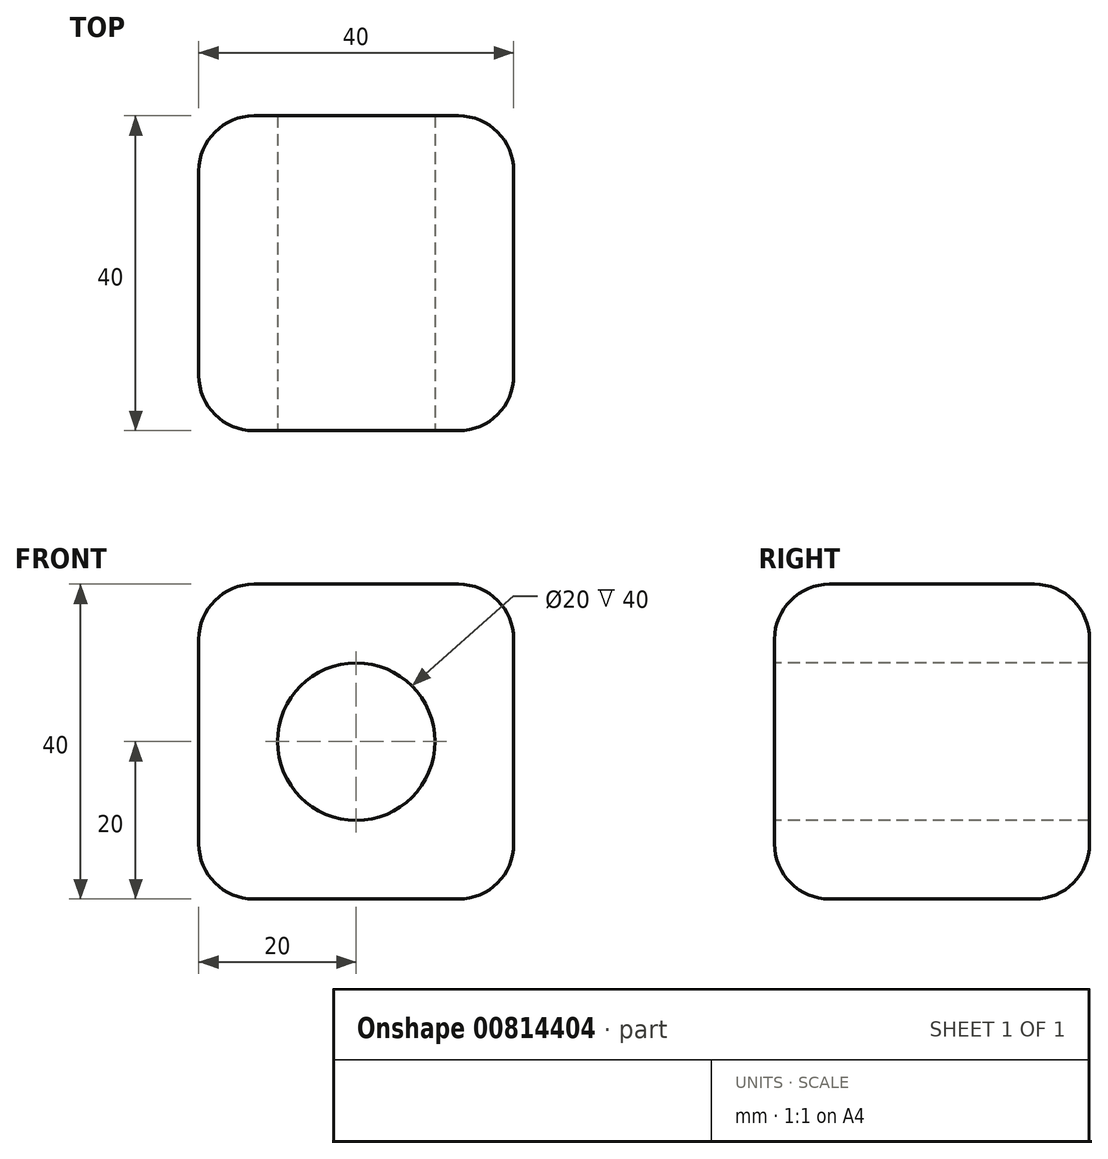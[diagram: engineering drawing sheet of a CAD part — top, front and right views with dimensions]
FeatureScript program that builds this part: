
annotation { "Feature Type Name" : "Feature", "Feature Type Description" : "" }
export const myFeature = defineFeature(function(context is Context, id is Id, definition is map)
    precondition{}
    {
        {
            var Q0;
            Q0=qCreatedBy(makeId("Front.planeOp"),FACE);
            var sketch = newSketch(context, id + "F0", { "sketchPlane" : qUnion([Q0])});
            skLineSegment(sketch, "E0.bottom", {"start": v(0, 40) * mm, "end": v(40, 40) * mm});
            skLineSegment(sketch, "E0.top", {"start": v(0, 0) * mm, "end": v(40, 0) * mm});
            skLineSegment(sketch, "E0.left", {"start": v(0, 40) * mm, "end": v(0, 0) * mm});
            skLineSegment(sketch, "E0.right", {"start": v(40, 40) * mm, "end": v(40, 0) * mm});
            skSolve(sketch);
        }
        {
            var Q0;
            Q0=makeQuery(id+"F0.imprint","IMPRINT",FACE,{"disambiguationData":[TD([[makeQuery(id+"F0.imprint","IMPRINT",EDGE,{"derivedFrom":sQuery(id+"F0.wireOp",EDGE,"E0.bottom")}),-1.0]])]});
            extrude(context, id + "F1", {"entities" : qUnion([Q0]), "depth" : 40 * mm, "offsetDistance" : 25 * mm});
        }
        {
            var Q0;
            Q0=makeQuery(id+"F1.opExtrude","SWEPT_FACE",FACE,{"disambiguationData":[OSD([sQuery(id+"F0.wireOp",EDGE,"E0.bottom")])]});
            var Q1;
            Q1=makeQuery(id+"F1.opExtrude","CAP_FACE",FACE,{"disambiguationData":[OSD([sQuery(id+"F0.wireOp",EDGE,"E0.bottom"),sQuery(id+"F0.wireOp",EDGE,"E0.top"),sQuery(id+"F0.wireOp",EDGE,"E0.left"),sQuery(id+"F0.wireOp",EDGE,"E0.right")])],"isStart":false});
            var Q2;
            Q2=makeQuery(id+"F1.opExtrude","SWEPT_FACE",FACE,{"disambiguationData":[OSD([sQuery(id+"F0.wireOp",EDGE,"E0.left")])]});
            var Q3;
            Q3=makeQuery(id+"F1.opExtrude","CAP_FACE",FACE,{"disambiguationData":[OSD([sQuery(id+"F0.wireOp",EDGE,"E0.bottom"),sQuery(id+"F0.wireOp",EDGE,"E0.top"),sQuery(id+"F0.wireOp",EDGE,"E0.left"),sQuery(id+"F0.wireOp",EDGE,"E0.right")])],"isStart":true});
            var Q4;
            Q4=makeQuery(id+"F1.opExtrude","SWEPT_FACE",FACE,{"disambiguationData":[OSD([sQuery(id+"F0.wireOp",EDGE,"E0.top")])]});
            fillet(context, id + "F2", {"entities" : qUnion([Q0, Q1, Q2, Q3, Q4]), "radius" : 7 * mm, "tangentPropagation" : true, "allowEdgeOverflow" : false});
        }
        {
            var Q0;
            Q0=makeQuery(id+"F1.opExtrude","CAP_FACE",FACE,{"disambiguationData":[OSD([sQuery(id+"F0.wireOp",EDGE,"E0.bottom"),sQuery(id+"F0.wireOp",EDGE,"E0.top"),sQuery(id+"F0.wireOp",EDGE,"E0.left"),sQuery(id+"F0.wireOp",EDGE,"E0.right")])],"isStart":false});
            var sketch = newSketch(context, id + "F3", { "sketchPlane" : qUnion([Q0])});
            skCircle(sketch, "E1", {"center": v(20, 20) * mm, "radius": 10 * mm});
            skSolve(sketch);
        }
        {
            var Q0;
            Q0=makeQuery(id+"F3.imprint","IMPRINT",FACE,{"disambiguationData":[TD([[makeQuery(id+"F3.imprint","IMPRINT",EDGE,{"derivedFrom":sQuery(id+"F3.wireOp",EDGE,"E1")}),1.0]])]});
            extrude(context, id + "F4", {"entities" : qUnion([Q0]), "operationType" : NewBodyOperationType.REMOVE, "oppositeDirection" : true, "depth" : 50 * mm, "offsetDistance" : 25 * mm});
        }
    });
